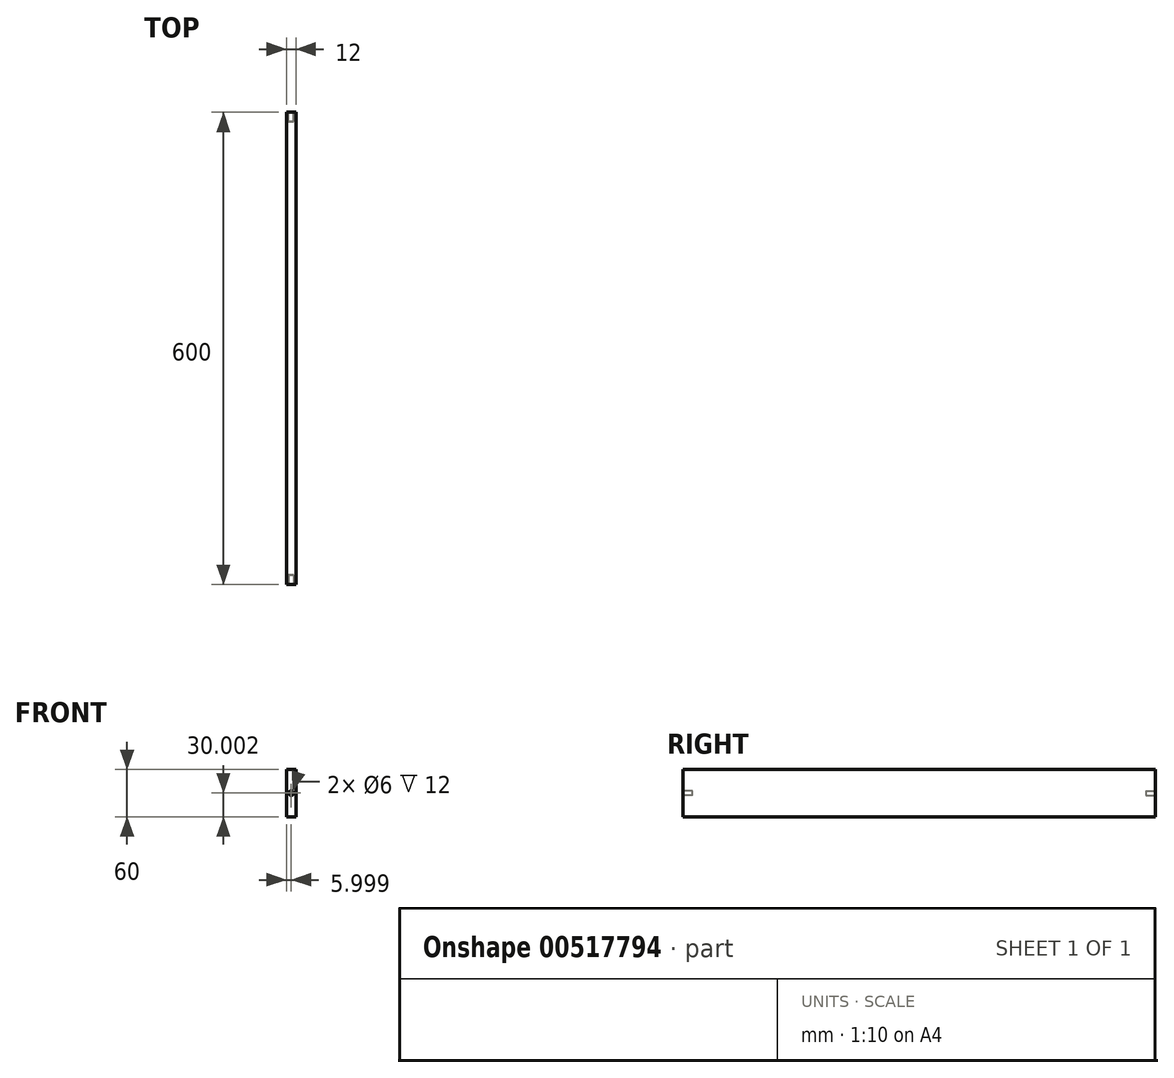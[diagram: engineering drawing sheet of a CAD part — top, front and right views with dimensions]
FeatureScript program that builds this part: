
annotation { "Feature Type Name" : "Feature", "Feature Type Description" : "" }
export const myFeature = defineFeature(function(context is Context, id is Id, definition is map)
    precondition{}
    {
        {
            var Q0;
            Q0=qCreatedBy(makeId("Front.planeOp"),FACE);
            var sketch = newSketch(context, id + "F0", { "sketchPlane" : qUnion([Q0])});
            skLineSegment(sketch, "E0.bottom", {"start": v(-62.3, 80.47) * mm, "end": v(-50.3, 80.47) * mm});
            skLineSegment(sketch, "E0.top", {"start": v(-62.3, 20.47) * mm, "end": v(-50.3, 20.47) * mm});
            skLineSegment(sketch, "E0.left", {"start": v(-62.3, 80.47) * mm, "end": v(-62.3, 20.47) * mm});
            skLineSegment(sketch, "E0.right", {"start": v(-50.3, 80.47) * mm, "end": v(-50.3, 20.47) * mm});
            skSolve(sketch);
        }
        {
            var Q0;
            Q0=makeQuery(id+"F0.imprint","IMPRINT",FACE,{"disambiguationData":[TD([[makeQuery(id+"F0.imprint","IMPRINT",EDGE,{"derivedFrom":sQuery(id+"F0.wireOp",EDGE,"E0.bottom")}),-1.0]])]});
            extrude(context, id + "F1", {"entities" : qUnion([Q0]), "endBound" : BoundingType.SYMMETRIC, "depth" : 600 * mm, "offsetDistance" : 25 * mm});
        }
        {
            var Q0;
            Q0=makeQuery(id+"F1.opExtrude","CAP_FACE",FACE,{"disambiguationData":[OSD([sQuery(id+"F0.wireOp",EDGE,"E0.bottom"),sQuery(id+"F0.wireOp",EDGE,"E0.top"),sQuery(id+"F0.wireOp",EDGE,"E0.left"),sQuery(id+"F0.wireOp",EDGE,"E0.right")])],"isStart":true});
            var sketch = newSketch(context, id + "F2", { "sketchPlane" : qUnion([Q0])});
            skCircle(sketch, "E1", {"center": v(56.3, 50.47) * mm, "radius": 3 * mm});
            skPoint(sketch, "E1.centerSnap0", {"position": v(56.3, 80.47) * mm});
            skSolve(sketch);
        }
        {
            var Q0;
            Q0=makeQuery(id+"F1.opExtrude","CAP_FACE",FACE,{"disambiguationData":[OSD([sQuery(id+"F0.wireOp",EDGE,"E0.bottom"),sQuery(id+"F0.wireOp",EDGE,"E0.top"),sQuery(id+"F0.wireOp",EDGE,"E0.left"),sQuery(id+"F0.wireOp",EDGE,"E0.right")])],"isStart":false});
            var sketch = newSketch(context, id + "F3", { "sketchPlane" : qUnion([Q0])});
            skSolve(sketch);
        }
        {
            var Q0;
            Q0=makeQuery(id+"F3.imprint","IMPRINT",FACE,{"disambiguationData":[TD([[makeQuery(id+"F3.imprint","IMPRINT",EDGE,{"derivedFrom":makeQuery(id+"F1.opExtrude","CAP_EDGE",EDGE,{"disambiguationData":[OSD([sQuery(id+"F0.wireOp",EDGE,"E0.bottom")])],"isStart":false})}),-1.0]])]});
            var sketch = newSketch(context, id + "F4", { "sketchPlane" : qUnion([Q0])});
            skLineSegment(sketch, "E2.0.0", {"start": v(-50.3, 80.47) * mm, "end": v(-62.3, 80.47) * mm});
            skLineSegment(sketch, "E2.0.1", {"start": v(-62.3, 80.47) * mm, "end": v(-62.3, 20.47) * mm});
            skLineSegment(sketch, "E2.0.2", {"start": v(-62.3, 20.47) * mm, "end": v(-50.3, 20.47) * mm});
            skLineSegment(sketch, "E2.0.3", {"start": v(-50.3, 20.47) * mm, "end": v(-50.3, 80.47) * mm});
            skSolve(sketch);
        }
        {
            var Q0;
            Q0=makeQuery(id+"F3.imprint","IMPRINT",FACE,{"disambiguationData":[TD([[makeQuery(id+"F3.imprint","IMPRINT",EDGE,{"derivedFrom":makeQuery(id+"F1.opExtrude","CAP_EDGE",EDGE,{"disambiguationData":[OSD([sQuery(id+"F0.wireOp",EDGE,"E0.bottom")])],"isStart":false})}),-1.0]])]});
            var sketch = newSketch(context, id + "F5", { "sketchPlane" : qUnion([Q0])});
            skCircle(sketch, "E3", {"center": v(-56.3, 50.47) * mm, "radius": 3 * mm});
            skSolve(sketch);
        }
        {
            var Q0;
            Q0=makeQuery(id+"F5.imprint","IMPRINT",FACE,{"disambiguationData":[TD([[makeQuery(id+"F5.imprint","IMPRINT",EDGE,{"derivedFrom":sQuery(id+"F5.wireOp",EDGE,"E3")}),1.0]])]});
            extrude(context, id + "F6", {"entities" : qUnion([Q0]), "operationType" : NewBodyOperationType.REMOVE, "oppositeDirection" : true, "depth" : 12 * mm, "offsetDistance" : 25 * mm});
        }
        {
            var Q0;
            Q0=makeQuery(id+"F2.imprint","IMPRINT",FACE,{"disambiguationData":[TD([[makeQuery(id+"F2.imprint","IMPRINT",EDGE,{"derivedFrom":sQuery(id+"F2.wireOp",EDGE,"E1")}),1.0]])]});
            var Q1;
            Q1=sQuery(id+"F2.wireOp",EDGE,"E1");
            extrude(context, id + "F7", {"entities" : qUnion([Q0]), "operationType" : NewBodyOperationType.REMOVE, "surfaceEntities" : qUnion([Q1]), "oppositeDirection" : true, "depth" : 12 * mm, "offsetDistance" : 25 * mm});
        }
    });
